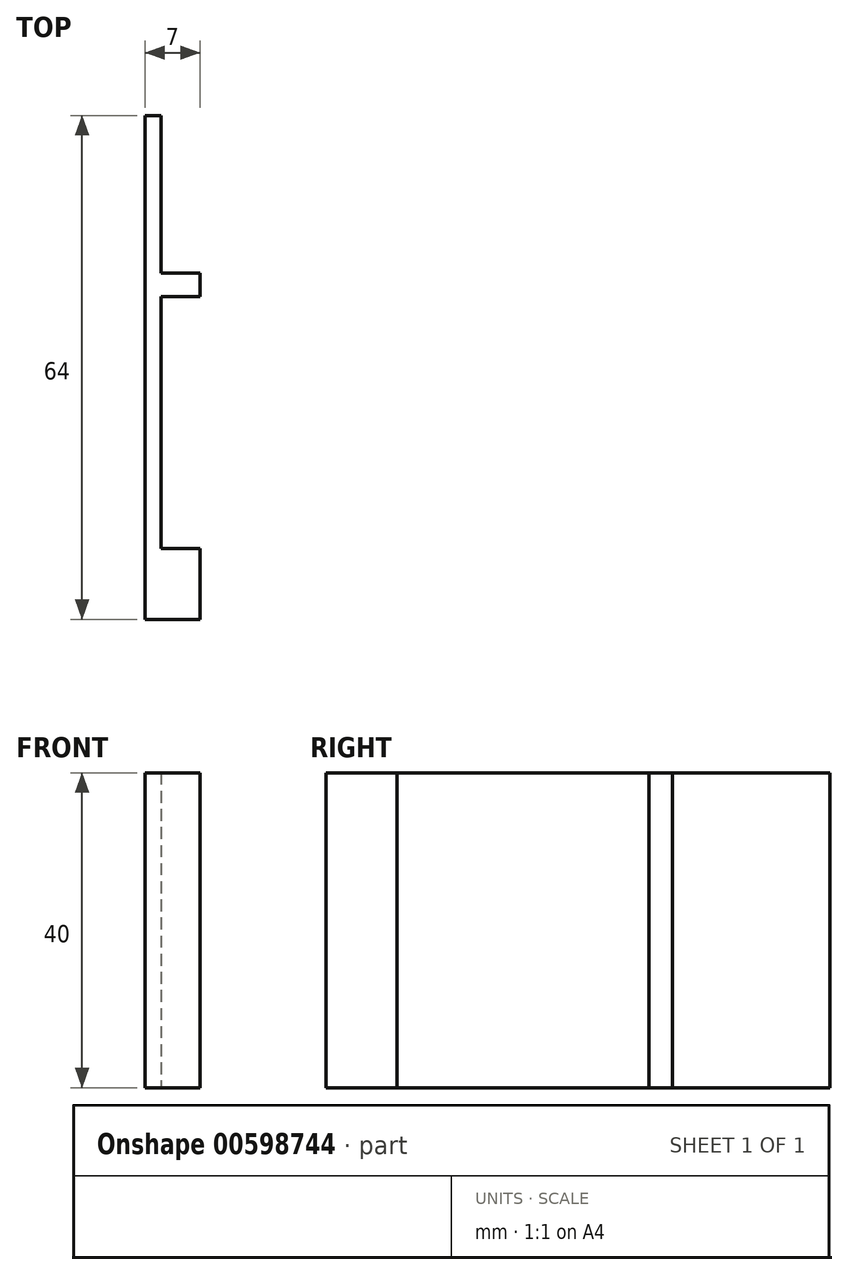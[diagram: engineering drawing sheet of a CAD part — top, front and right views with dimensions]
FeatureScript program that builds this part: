
annotation { "Feature Type Name" : "Feature", "Feature Type Description" : "" }
export const myFeature = defineFeature(function(context is Context, id is Id, definition is map)
    precondition{}
    {
        {
            var Q0;
            Q0=qCreatedBy(makeId("Top.planeOp"),FACE);
            var sketch = newSketch(context, id + "F0", { "sketchPlane" : qUnion([Q0])});
            skLineSegment(sketch, "E0.bottom", {"start": v(-1, 32) * mm, "end": v(1, 32) * mm});
            skLineSegment(sketch, "E0.top", {"start": v(-1, -32) * mm, "end": v(1, -32) * mm});
            skLineSegment(sketch, "E0.left", {"start": v(-1, 32) * mm, "end": v(-1, -32) * mm});
            skLineSegment(sketch, "E0.right", {"start": v(1, 32) * mm, "end": v(1, -32) * mm});
            skPoint(sketch, "E0.middle", {"position": v(0, 0) * mm});
            skLineSegment(sketch, "E1.bottom", {"start": v(1, -32) * mm, "end": v(6, -32) * mm});
            skLineSegment(sketch, "E1.top", {"start": v(1, -23) * mm, "end": v(6, -23) * mm});
            skLineSegment(sketch, "E1.left", {"start": v(1, -32) * mm, "end": v(1, -23) * mm});
            skLineSegment(sketch, "E1.right", {"start": v(6, -32) * mm, "end": v(6, -23) * mm});
            skLineSegment(sketch, "E2", {"start": v(1, 32) * mm, "end": v(1, 12) * mm});
            skLineSegment(sketch, "E3.bottom", {"start": v(1, 12) * mm, "end": v(6, 12) * mm});
            skLineSegment(sketch, "E3.top", {"start": v(1, 9) * mm, "end": v(6, 9) * mm});
            skLineSegment(sketch, "E3.left", {"start": v(1, 12) * mm, "end": v(1, 9) * mm});
            skLineSegment(sketch, "E3.right", {"start": v(6, 12) * mm, "end": v(6, 9) * mm});
            skSolve(sketch);
        }
        {
            var Q0;
            Q0=makeQuery(id+"F0.imprint","IMPRINT",FACE,{"disambiguationData":[TD([[makeQuery(id+"F0.imprint","IMPRINT",EDGE,{"derivedFrom":sQuery(id+"F0.wireOp",EDGE,"E0.bottom")}),-1.0]])]});
            var Q1;
            Q1=makeQuery(id+"F0.imprint","IMPRINT",FACE,{"disambiguationData":[TD([[makeQuery(id+"F0.imprint","IMPRINT",EDGE,{"derivedFrom":sQuery(id+"F0.wireOp",EDGE,"E1.bottom")}),1.0]])]});
            var Q2;
            Q2=makeQuery(id+"F0.imprint","IMPRINT",FACE,{"disambiguationData":[TD([[makeQuery(id+"F0.imprint","IMPRINT",EDGE,{"derivedFrom":sQuery(id+"F0.wireOp",EDGE,"E3.bottom")}),-1.0]])]});
            extrude(context, id + "F1", {"entities" : qUnion([Q0, Q1, Q2]), "depth" : 40 * mm, "offsetDistance" : 25.4 * mm});
        }
    });
